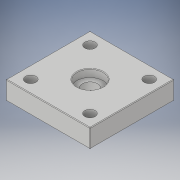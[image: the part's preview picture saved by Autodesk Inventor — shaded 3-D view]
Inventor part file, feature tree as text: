
AUTODESK INVENTOR PART (.ipt)
format: ipt  version: 2019 (Build 230136000, 136)  size: 157,184 bytes
history: native  units: mm
features: sketch x4, extrude x2, hole x2, fillet x2
ambient origin geometry x8: Origin, YZ Plane, XZ Plane, XY Plane, X Axis, Y Axis, Z Axis, Center Point
bodies: Solid1 (feature_tree)
feature tree (10):
  extrude  "Extrusion1"  Depth=36.0mm
  hole  "Hole2"  [1 undecoded]
  hole  "Hole1"  [1 undecoded]
  fillet  "Fillet1"  Radius=0.25mm
  fillet  "Fillet2"  Radius=25.374mm
  extrude  "Extrusion2"  Depth=1.5875mm TaperAngle=0.0deg
  sketch  "Sketch1"  dims[d0=36.0mm d1=36.0mm]
  sketch  "Sketch2"  dims[d2=7.9375mm d3=0.0mm]
  sketch  "Sketch3"  dims[d4=6.528mm d5=6.0mm d6=11.113mm d7=3.25mm d8=14.3117mm d9=19.05mm d10=20.594885mm d11=25.4mm]
  sketch  "Sketch4"  dims[d12=4.496mm d13=8.331mm d14=7.145mm d15=3.505mm d16=14.3117mm d17=12.3mm d18=20.594885mm d19=0.25mm d20=0.25mm d21=25.374mm d22=1.5875mm d23=0.0mm d24=1.0mm d25=1.0mm d26=1.0mm d27=0.15mm d28=0.25mm d29=0.375mm d30=14.3117mm d31=0.75mm d32=20.594885mm d33=0.0625mm d34=0.75mm d35=0.375mm]
note: 2 required parameter values undecoded (feature->parameter linkage not recoverable at this tier; creation-order binding heuristic only, values carry confidence <= 0.55)
